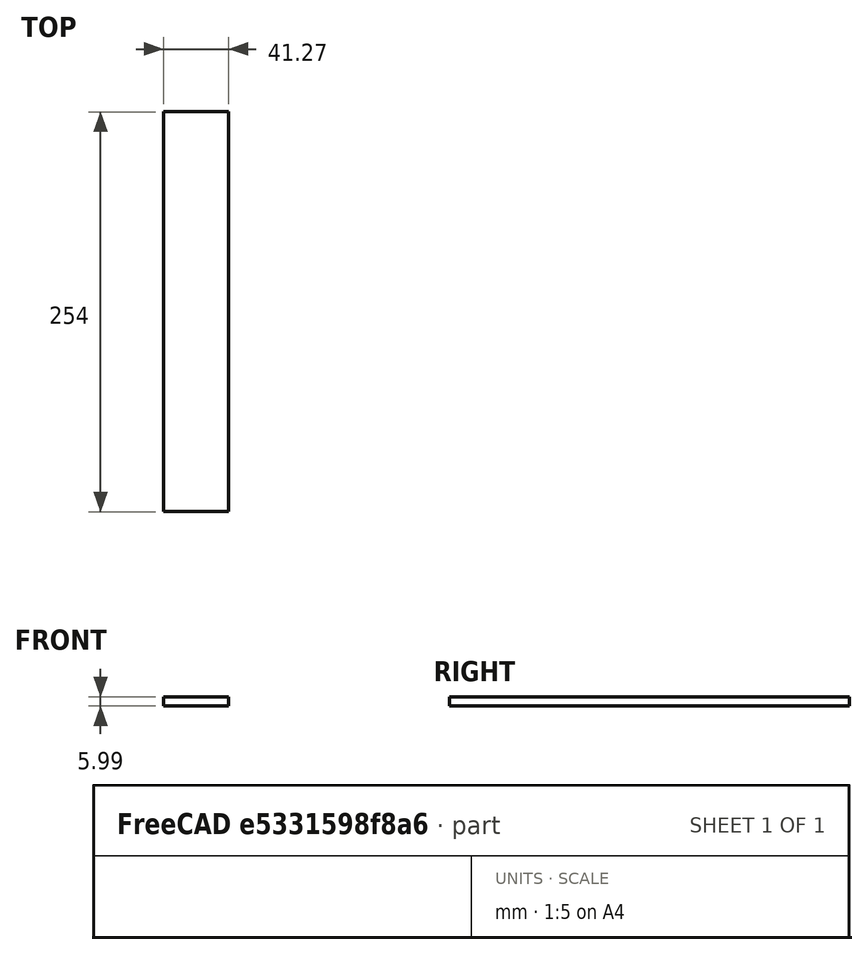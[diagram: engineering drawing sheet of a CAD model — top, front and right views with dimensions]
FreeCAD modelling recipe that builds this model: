
FCSTD DOCUMENT  (FreeCAD 0.19R24267 (Git))
Label: Inv1-P5
License: All rights reserved
LicenseURL: http://en.wikipedia.org/wiki/All_rights_reserved
objects: TechDraw::DrawViewDimension×3, TechDraw::DrawProjGroupItem×2, TechDraw::DrawHatch×2, TechDraw::DrawViewAnnotation×2, Sketcher::SketchObject×1, Part::Extrusion×1, TechDraw::DrawSVGTemplate×1, TechDraw::DrawProjGroup×1, TechDraw::DrawPage×1
note: 2 computed .brp shape members not serialized (recipe doc carries the construction recipe); baked Part::Feature solids carry a one-line shape summary decoded from their .brp

FEATURE [Sketcher::SketchObject] Sketch
  FullyConstrained = false
  sketch-geometry (4):
    g0: LineSegment StartX=-23.9627 StartY=114.965 StartZ=0 EndX=17.3123 EndY=114.965 EndZ=0
    g1: LineSegment StartX=17.3123 StartY=114.965 StartZ=0 EndX=17.3123 EndY=-139.035 EndZ=0
    g2: LineSegment StartX=17.3123 StartY=-139.035 StartZ=0 EndX=-23.9627 EndY=-139.035 EndZ=0
    g3: LineSegment StartX=-23.9627 StartY=-139.035 StartZ=0 EndX=-23.9627 EndY=114.965 EndZ=0
  constraints (10):
    c: Coincident(g0,g1)
    c: Coincident(g1,g2)
    c: Coincident(g2,g3)
    c: Coincident(g3,g0)
    c: Horizontal(g0)
    c: Horizontal(g2)
    c: Vertical(g1)
    c: Vertical(g3)
    c: DistanceY(g3,g3) = 254
    c: DistanceX(g0,g0) = 41.275
FEATURE [Part::Extrusion] Extrude
  Base = -> Sketch
  Dir = (0,0,1)
  DirMode = 2
  FaceMakerClass = Part::FaceMakerBullseye
  LengthFwd = 5.9944
  LengthRev = 0
  Solid = true
  Symmetric = false
FEATURE [TechDraw::DrawSVGTemplate] Template
  Height = 215.9
  Orientation = 1
  Width = 279.4
FEATURE [TechDraw::DrawProjGroupItem] ProjItem  label="Front"
  CoarseView = false
  Direction = (0,0,1)
  Focus = 100
  HardHidden = false
  IsoCount = 0
  IsoHidden = false
  IsoVisible = false
  LockPosition = true
  Perspective = false
  Rotation = 0
  RotationVector = (1,0,0)
  Scale = 0.5
  ScaleType = 2
  SeamHidden = false
  SeamVisible = true
  SmoothHidden = false
  SmoothVisible = true
  Source = -> [Extrude]
  Type = 0
  X = 0
  XDirection = (1,0,0)
  Y = 0
FEATURE [TechDraw::DrawProjGroupItem] ProjItem001  label="Left"
  CoarseView = false
  Direction = (-1,0,1e-16)
  Focus = 100
  HardHidden = false
  IsoCount = 0
  IsoHidden = false
  IsoVisible = false
  LockPosition = false
  Perspective = false
  Rotation = 0
  RotationVector = (1,0,0)
  Scale = 0.5
  ScaleType = 2
  SeamHidden = false
  SeamVisible = true
  SmoothHidden = false
  SmoothVisible = true
  Source = -> [Extrude]
  Type = 1
  X = 50.4139
  XDirection = (1e-16,0,1)
  Y = 0
FEATURE [TechDraw::DrawProjGroup] ProjGroup
  Anchor = -> ProjItem
  AutoDistribute = true
  LockPosition = false
  ProjectionType = 0
  Rotation = 0
  Scale = 0.5
  ScaleType = 0
  Source = -> [Extrude]
  Views = -> [ProjItem,ProjItem001]
  X = 132.354
  Y = 107.95
  spacingX = 15.0114
  spacingY = 15.0114
FEATURE [TechDraw::DrawHatch] Hatch  label="HatchF0"
  HatchPattern = <path>
  Source = -> ProjItem [Face0]
FEATURE [TechDraw::DrawHatch] Hatch001  label="Hatch001F0"
  HatchPattern = <path>
  Source = -> ProjItem001 [Face0]
FEATURE [TechDraw::DrawViewAnnotation] Annotation
  Font = osifont
  LineSpace = 80
  LockPosition = false
  MaxWidth = -1
  Rotation = 0
  ScaleType = 0
  Text = Figure S1 (Inverted 1) | Panel 5 [camera port side] | Quantity: 2
  TextSize = 5.0038
  TextStyle = 0
  X = 37.6458
  Y = 195.58
FEATURE [TechDraw::DrawViewAnnotation] Annotation001
  Font = osifont
  LineSpace = 80
  LockPosition = false
  MaxWidth = -1
  Rotation = 0
  ScaleType = 0
  Text = Units: Inches
  TextSize = 5.0038
  TextStyle = 0
  X = 259.08
  Y = 5.08
FEATURE [TechDraw::DrawViewDimension] Dimension
  Arbitrary = false
  ArbitraryTolerances = false
  EqualTolerance = true
  FormatSpec = %.3f
  FormatSpecOverTolerance = %+.3f
  FormatSpecUnderTolerance = %+.3f
  Inverted = false
  LockPosition = false
  MeasureType = 1
  OverTolerance = 0
  References2D = -> [ProjItem]
  Rotation = 0
  ScaleType = 0
  TheoreticalExact = false
  Type = 2
  UnderTolerance = 0
  X = 21.2015
  Y = -0.294129
FEATURE [TechDraw::DrawViewDimension] Dimension001
  Arbitrary = false
  ArbitraryTolerances = false
  EqualTolerance = true
  FormatSpec = %.3f
  FormatSpecOverTolerance = %+.3f
  FormatSpecUnderTolerance = %+.3f
  Inverted = false
  LockPosition = false
  MeasureType = 1
  OverTolerance = 0
  References2D = -> [ProjItem001]
  Rotation = 0
  ScaleType = 0
  TheoreticalExact = false
  Type = 1
  UnderTolerance = 0
  X = 18.1889
  Y = 34.9695
FEATURE [TechDraw::DrawViewDimension] Dimension002
  Arbitrary = false
  ArbitraryTolerances = false
  EqualTolerance = true
  FormatSpec = %.3f
  FormatSpecOverTolerance = %+.3f
  FormatSpecUnderTolerance = %+.3f
  Inverted = false
  LockPosition = false
  MeasureType = 1
  OverTolerance = 0
  References2D = -> [ProjItem]
  Rotation = 0
  ScaleType = 0
  TheoreticalExact = false
  Type = 1
  UnderTolerance = 0
  X = -0.45884
  Y = 76.2112
FEATURE [TechDraw::DrawPage] Page
  KeepUpdated = true
  NextBalloonIndex = 1
  ProjectionType = 0
  Template = -> Template
  Views = -> [ProjGroup,Annotation,Annotation001,Dimension,Dimension001,Dimension002]
note: 2 file-system paths scrubbed to <path> (originals preserved in the JSON sidecar)
